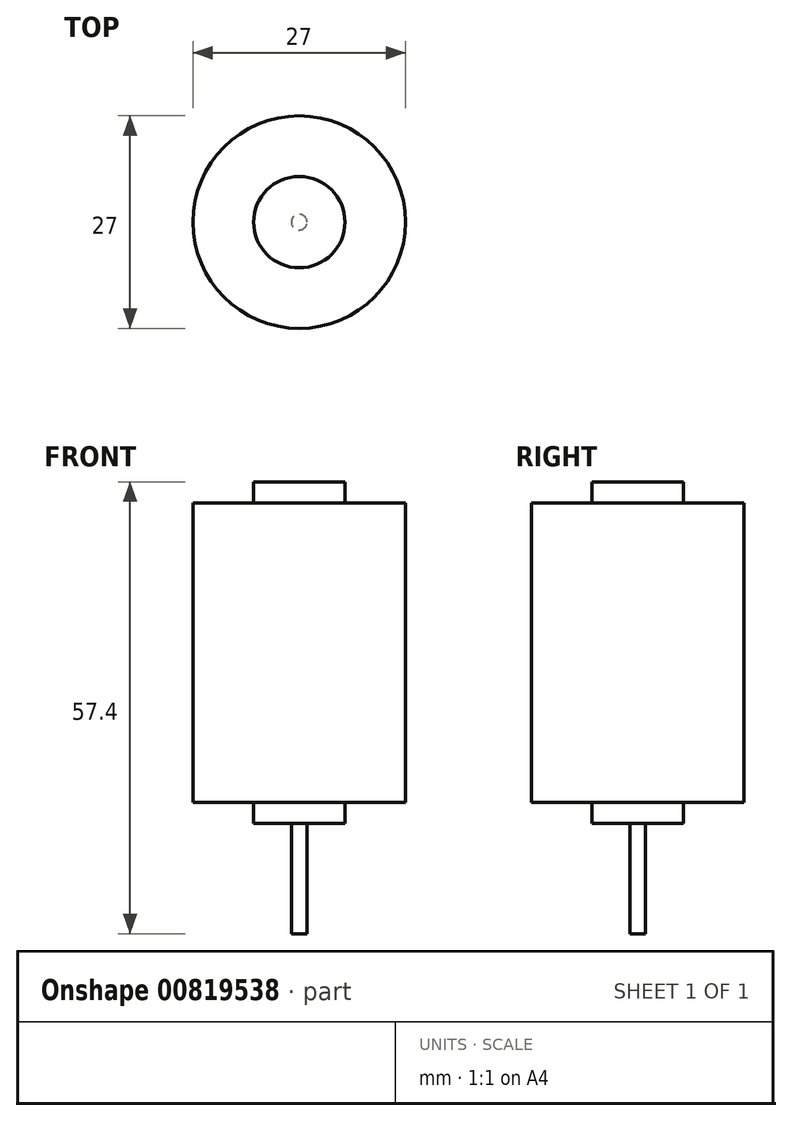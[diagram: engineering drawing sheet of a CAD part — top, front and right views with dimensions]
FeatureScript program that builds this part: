
annotation { "Feature Type Name" : "Feature", "Feature Type Description" : "" }
export const myFeature = defineFeature(function(context is Context, id is Id, definition is map)
    precondition{}
    {
        {
            var Q0;
            Q0=qCreatedBy(makeId("Right.planeOp"),FACE);
            var sketch = newSketch(context, id + "F0", { "sketchPlane" : qUnion([Q0])});
            skLineSegment(sketch, "E0", {"start": v(-26.56, 11.7) * mm, "end": v(-26.56, 9) * mm});
            skLineSegment(sketch, "E1", {"start": v(-26.56, 9) * mm, "end": v(-18.86, 9) * mm});
            skLineSegment(sketch, "E2", {"start": v(-18.86, 9) * mm, "end": v(-18.86, -29) * mm});
            skLineSegment(sketch, "E3", {"start": v(-18.86, -29) * mm, "end": v(-26.56, -29) * mm});
            skLineSegment(sketch, "E4", {"start": v(-26.56, -29) * mm, "end": v(-26.56, -31.7) * mm});
            skLineSegment(sketch, "E5", {"start": v(-26.56, -31.7) * mm, "end": v(-31.36, -31.7) * mm});
            skLineSegment(sketch, "E6", {"start": v(-31.36, -31.7) * mm, "end": v(-31.36, -45.7) * mm});
            skLineSegment(sketch, "E7", {"start": v(-31.36, -45.7) * mm, "end": v(-32.36, -45.7) * mm});
            skLineSegment(sketch, "E8", {"start": v(-32.36, -45.7) * mm, "end": v(-32.36, 11.7) * mm});
            skLineSegment(sketch, "E9", {"start": v(-32.36, 11.7) * mm, "end": v(-26.56, 11.7) * mm});
            skSolve(sketch);
        }
        {
            var Q0;
            Q0=makeQuery(id+"F0.imprint","IMPRINT",FACE,{"disambiguationData":[TD([[makeQuery(id+"F0.imprint","IMPRINT",EDGE,{"derivedFrom":sQuery(id+"F0.wireOp",EDGE,"E0")}),-1.0]])]});
            var Q1;
            Q1=sQuery(id+"F0.wireOp",EDGE,"E8");
            revolve(context, id + "F1", {"surfaceOperationType" : NewSurfaceOperationType.NEW, "entities" : qUnion([Q0]), "axis" : qUnion([Q1]), "revolveType" : RevolveType.FULL});
        }
    });
